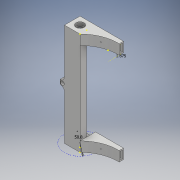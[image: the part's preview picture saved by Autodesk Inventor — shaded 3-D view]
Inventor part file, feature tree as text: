
AUTODESK INVENTOR PART (.ipt)
format: ipt  version: 2018 (Build 220112000, 112)  size: 259,584 bytes
history: native  units: mm
features: sketch x18, extrude x12, fillet x2
ambient origin geometry x8: Origin, YZ Plane, XZ Plane, XY Plane, X Axis, Y Axis, Z Axis, Center Point
bodies: Solid1 (feature_tree)
feature tree (32):
  extrude  "Extrusion1"  Depth=165.0mm
  extrude  "Extrusion2"  Depth=7.0mm
  sketch  "Sketch3"  dims[d5=7.0mm d6=22.0mm d7=0.0mm]
  extrude  "Extrusion3"  Depth=7.0mm TaperAngle=0.0deg
  extrude  "Extrusion4"  Depth=5.0mm TaperAngle=0.0deg
  extrude  "Extrusion5"  Depth=10.0mm
  sketch  "Sketch7"  dims[d18=7.5mm d19=0.0mm d20=2.0mm]
  sketch  "Sketch8"  dims[d21=16.0mm d22=16.0mm]
  extrude  "Extrusion6"  Depth=5.0mm
  fillet  "Fillet1"  Radius=5.0mm
  extrude  "Extrusion7"  Depth=2.0mm
  extrude  "Extrusion8"  Depth=16.0mm
  sketch  "Sketch12"  dims[d31=40.0mm d32=0.0mm d33=1.875mm]
  extrude  "Extrusion9"  Depth=3.5mm
  sketch  "Sketch14"  dims[d35=60.0mm]
  sketch  "Sketch15"  dims[d36=165.0mm d37=0.0mm]
  extrude  "Extrusion10"  Depth=3.25mm
  extrude  "Extrusion11"  Depth=12.25mm
  fillet  "Fillet2"  Radius=3.25mm
  extrude  "Extrusion12"  Depth=1.875mm
  sketch  "Sketch1"  dims[d0=25.0mm d1=165.0mm]
  sketch  "Sketch2"  dims[d2=3.0mm d3=0.0mm d4=7.0mm]
  sketch  "Sketch4"  dims[d8=13.0mm d9=5.0mm d10=0.0mm]
  sketch  "Sketch5"  dims[d11=5.0mm d12=0.0mm d13=10.0mm]
  sketch  "Sketch6"  dims[d14=165.0mm d15=0.0mm d16=5.0mm d17=5.0mm]
  sketch  "Sketch9"  dims[d23=45.0mm d24=0.0mm d25=3.5mm]
  sketch  "Sketch10"  dims[d26=12.25mm d27=3.25mm]
  sketch  "Sketch11"  dims[d28=3.5mm d29=12.25mm d30=3.25mm]
  sketch  "Sketch13"  dims[d34=7.0mm]
  sketch  "Sketch16"  dims[d38=50.8mm]
  sketch  "Sketch17"  dims[d39=7.0mm]
  sketch  "Sketch18"  dims[d40=3.5mm d41=3.5mm d42=10.5mm d43=0.0mm d44=6.35mm d45=10.5mm d46=0.0mm d47=7.0mm d48=25.0mm d49=1.5mm d50=25.0mm d51=1.5mm d52=25.0mm d53=0.0mm]
